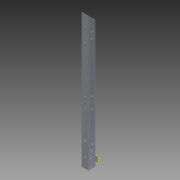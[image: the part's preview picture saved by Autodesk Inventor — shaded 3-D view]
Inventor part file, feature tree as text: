
AUTODESK INVENTOR PART (.ipt)
format: ipt  version: 2013 (Build 170138000, 138)  size: 162,816 bytes
history: native  units: in
note: dims shown in document units (in); Inventor stores cm internally (conversion verified against a paired STEP export)
features: extrude x11, sketch x10, reference x10, plane x1
ambient origin geometry x8: Origin, YZ Plane, XZ Plane, XY Plane, X Axis, Y Axis, Z Axis, Center Point
bodies: Solid1 (feature_tree)
feature tree (32):
  extrude  "Extrusion1"  Depth=1.0in
  extrude  "Extrusion3"  Depth=19.5in TaperAngle=0.0deg
  plane  "Work Plane1"
  extrude  "Extrusion4"  Depth=0.266in
  extrude  "Extrusion5"  Depth=1.5in
  extrude  "Extrusion6"  Depth=0.25in
  extrude  "Extrusion9"  Depth=0.266in
  extrude  "Extrusion10"  Depth=2.5in
  extrude  "Extrusion11"  Depth=0.25in
  extrude  "Extrusion12"  Depth=1.0in TaperAngle=0.0deg
  extrude  "Extrusion13"  Depth=1.0in TaperAngle=0.0deg
  extrude  "Extrusion14"  Depth=1.0in TaperAngle=0.0deg
  sketch  "Sketch1"  dims[d0=1.0in d2=1.0in]
  sketch  "Sketch3"  dims[d3=0.875in d4=19.5in d5=0.0in]
  sketch  "Sketch4"  dims[d7=45.0deg d10=0.266in]
  sketch  "Sketch5"  dims[d11=0.266in d12=1.5in]
  reference  "Reference3"
  reference  "Reference4"
  sketch  "Sketch8"  dims[d13=0.25in d14=0.25in]
  reference  "Reference12"
  reference  "Reference13"
  reference  "Reference14"
  reference  "Reference15"
  sketch  "Sketch9"  dims[d15=2.5in d16=0.266in]
  reference  "Reference16"
  reference  "Reference17"
  reference  "Reference18"
  reference  "Reference19"
  sketch  "Sketch10"  dims[d17=0.266in d18=2.5in]
  sketch  "Sketch11"  dims[d19=1.5in d20=0.25in]
  sketch  "Sketch12"  dims[d21=0.25in d22=1.0in d23=0.0in]
  sketch  "Sketch13"  dims[d24=1.0in d25=0.0in d26=1.0in d27=0.0in d28=1.0in d29=0.0in d34=1.0in d35=0.0in d36=1.0in d37=0.0in d38=0.0625in d39=0.0in d40=0.0625in d41=0.0in d42=0.0625in d43=0.0in d44=0.0625in d45=0.0in]
